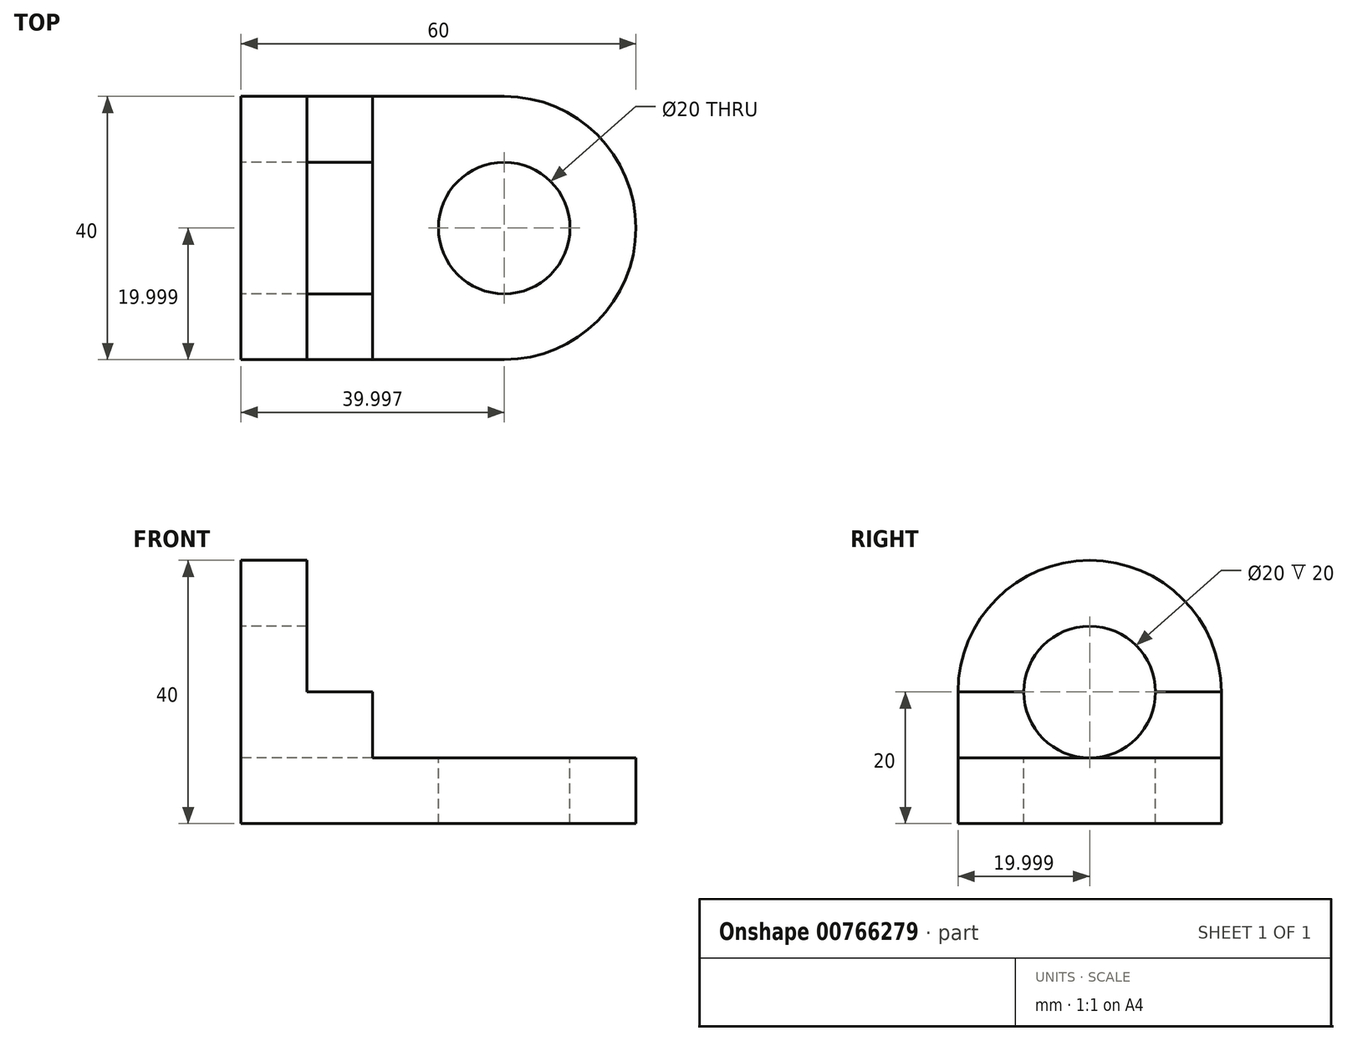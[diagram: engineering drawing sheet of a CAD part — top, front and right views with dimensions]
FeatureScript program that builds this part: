
annotation { "Feature Type Name" : "Feature", "Feature Type Description" : "" }
export const myFeature = defineFeature(function(context is Context, id is Id, definition is map)
    precondition{}
    {
        {
            var Q0;
            Q0=qCreatedBy(makeId("Top.planeOp"),FACE);
            var sketch = newSketch(context, id + "F0", { "sketchPlane" : qUnion([Q0])});
            skLineSegment(sketch, "E0.bottom", {"start": v(-26.43, 18.86) * mm, "end": v(33.57, 18.86) * mm});
            skLineSegment(sketch, "E0.top", {"start": v(-26.43, -21.14) * mm, "end": v(33.57, -21.14) * mm});
            skLineSegment(sketch, "E0.left", {"start": v(-26.43, 18.86) * mm, "end": v(-26.43, -21.14) * mm});
            skLineSegment(sketch, "E0.right", {"start": v(33.57, 18.86) * mm, "end": v(33.57, -21.14) * mm});
            skSolve(sketch);
        }
        {
            var Q0;
            Q0=makeQuery(id+"F0.imprint","IMPRINT",FACE,{"disambiguationData":[TD([[makeQuery(id+"F0.imprint","IMPRINT",EDGE,{"derivedFrom":sQuery(id+"F0.wireOp",EDGE,"E0.bottom")}),-1.0]])]});
            extrude(context, id + "F1", {"entities" : qUnion([Q0]), "depth" : 10 * mm, "offsetDistance" : 25.4 * mm});
        }
        {
            var Q0;
            Q0=makeQuery(id+"F1.opExtrude","CAP_FACE",FACE,{"disambiguationData":[OSD([sQuery(id+"F0.wireOp",EDGE,"E0.bottom"),sQuery(id+"F0.wireOp",EDGE,"E0.top"),sQuery(id+"F0.wireOp",EDGE,"E0.left"),sQuery(id+"F0.wireOp",EDGE,"E0.right")])],"isStart":false});
            var sketch = newSketch(context, id + "F2", { "sketchPlane" : qUnion([Q0])});
            skLineSegment(sketch, "E1", {"start": v(33.57, -1.14) * mm, "end": v(13.57, -1.14) * mm});
            skCircle(sketch, "E2", {"center": v(13.57, -1.14) * mm, "radius": 10 * mm});
            skSolve(sketch);
        }
        {
            var Q0;
            Q0=makeQuery(id+"F2.imprint","IMPRINT",FACE,{"disambiguationData":[TD([[makeQuery(id+"F2.imprint","IMPRINT",EDGE,{"derivedFrom":sQuery(id+"F2.wireOp",EDGE,"E2")}),1.0]])]});
            extrude(context, id + "F3", {"entities" : qUnion([Q0]), "operationType" : NewBodyOperationType.REMOVE, "oppositeDirection" : true, "depth" : 10 * mm, "offsetDistance" : 25.4 * mm});
        }
        {
            var Q0;
            Q0=makeQuery(id+"F1.opExtrude","SWEPT_EDGE",EDGE,{"disambiguationData":[OSD([sQuery(id+"F0.wireOp",EDGE,"E0.bottom"),sQuery(id+"F0.wireOp",EDGE,"E0.right")])]});
            var Q1;
            Q1=makeQuery(id+"F1.opExtrude","SWEPT_EDGE",EDGE,{"disambiguationData":[OSD([sQuery(id+"F0.wireOp",EDGE,"E0.top"),sQuery(id+"F0.wireOp",EDGE,"E0.right")])]});
            fillet(context, id + "F4", {"entities" : qUnion([Q0, Q1]), "radius" : 20 * mm, "tangentPropagation" : true, "allowEdgeOverflow" : false});
        }
        {
            var Q0;
            Q0=makeQuery(id+"F1.opExtrude","CAP_FACE",FACE,{"disambiguationData":[OSD([sQuery(id+"F0.wireOp",EDGE,"E0.bottom"),sQuery(id+"F0.wireOp",EDGE,"E0.top"),sQuery(id+"F0.wireOp",EDGE,"E0.left"),sQuery(id+"F0.wireOp",EDGE,"E0.right")])],"isStart":false});
            var sketch = newSketch(context, id + "F5", { "sketchPlane" : qUnion([Q0])});
            skLineSegment(sketch, "E3.bottom", {"start": v(-26.43, 18.86) * mm, "end": v(-6.43, 18.86) * mm});
            skLineSegment(sketch, "E3.top", {"start": v(-26.43, -21.14) * mm, "end": v(-6.43, -21.14) * mm});
            skLineSegment(sketch, "E3.left", {"start": v(-26.43, 18.86) * mm, "end": v(-26.43, -21.14) * mm});
            skLineSegment(sketch, "E3.right", {"start": v(-6.43, 18.86) * mm, "end": v(-6.43, -21.14) * mm});
            skSolve(sketch);
        }
        {
            var Q0;
            Q0=makeQuery(id+"F5.imprint","IMPRINT",FACE,{"disambiguationData":[TD([[makeQuery(id+"F5.imprint","IMPRINT",EDGE,{"derivedFrom":sQuery(id+"F5.wireOp",EDGE,"E3.bottom")}),-1.0]])]});
            extrude(context, id + "F6", {"entities" : qUnion([Q0]), "operationType" : NewBodyOperationType.ADD, "depth" : 10 * mm, "offsetDistance" : 25.4 * mm});
        }
        {
            var Q0;
            Q0=makeQuery(id+"F6.opExtrude","CAP_FACE",FACE,{"disambiguationData":[OSD([sQuery(id+"F5.wireOp",EDGE,"E3.bottom"),sQuery(id+"F5.wireOp",EDGE,"E3.top"),sQuery(id+"F5.wireOp",EDGE,"E3.left"),sQuery(id+"F5.wireOp",EDGE,"E3.right")])],"isStart":false});
            var sketch = newSketch(context, id + "F7", { "sketchPlane" : qUnion([Q0])});
            skLineSegment(sketch, "E4.bottom", {"start": v(-26.43, 18.86) * mm, "end": v(-16.43, 18.86) * mm});
            skLineSegment(sketch, "E4.top", {"start": v(-26.43, -21.14) * mm, "end": v(-16.43, -21.14) * mm});
            skLineSegment(sketch, "E4.left", {"start": v(-26.43, 18.86) * mm, "end": v(-26.43, -21.14) * mm});
            skLineSegment(sketch, "E4.right", {"start": v(-16.43, 18.86) * mm, "end": v(-16.43, -21.14) * mm});
            skSolve(sketch);
        }
        {
            var Q0;
            Q0=makeQuery(id+"F7.imprint","IMPRINT",FACE,{"disambiguationData":[TD([[makeQuery(id+"F7.imprint","IMPRINT",EDGE,{"derivedFrom":sQuery(id+"F7.wireOp",EDGE,"E4.bottom")}),-1.0]])]});
            extrude(context, id + "F8", {"entities" : qUnion([Q0]), "operationType" : NewBodyOperationType.ADD, "depth" : 20 * mm, "offsetDistance" : 25.4 * mm});
        }
        {
            var Q0;
            Q0=makeQuery(id+"F8.boolean.opBoolean","MERGE",FACE,{"derivedFrom":[makeQuery(id+"F6.boolean.opBoolean","MERGE",FACE,{"derivedFrom":[makeQuery(id+"F1.opExtrude","SWEPT_FACE",FACE,{"disambiguationData":[OSD([sQuery(id+"F0.wireOp",EDGE,"E0.left")])]}),makeQuery(id+"F6.opExtrude","SWEPT_FACE",FACE,{"disambiguationData":[OSD([sQuery(id+"F5.wireOp",EDGE,"E3.left")])]})]}),makeQuery(id+"F8.opExtrude","SWEPT_FACE",FACE,{"disambiguationData":[OSD([sQuery(id+"F7.wireOp",EDGE,"E4.left")])]})]});
            var sketch = newSketch(context, id + "F9", { "sketchPlane" : qUnion([Q0])});
            skCircle(sketch, "E5", {"center": v(1.14, 20) * mm, "radius": 10 * mm});
            skPoint(sketch, "E5.centerSnap0", {"position": v(21.14, 20) * mm});
            skPoint(sketch, "E5.centerSnap1", {"position": v(1.14, 40) * mm});
            skSolve(sketch);
        }
        {
            var Q0;
            Q0=makeQuery(id+"F9.imprint","IMPRINT",FACE,{"disambiguationData":[TD([[makeQuery(id+"F9.imprint","IMPRINT",EDGE,{"derivedFrom":sQuery(id+"F9.wireOp",EDGE,"E5")}),1.0]])]});
            extrude(context, id + "F10", {"entities" : qUnion([Q0]), "operationType" : NewBodyOperationType.REMOVE, "oppositeDirection" : true, "depth" : 20 * mm, "offsetDistance" : 25.4 * mm});
        }
        {
            var Q0;
            Q0=makeQuery(id+"F8.opExtrude","CAP_EDGE",EDGE,{"disambiguationData":[OSD([sQuery(id+"F7.wireOp",EDGE,"E4.top")])],"isStart":false});
            var Q1;
            Q1=makeQuery(id+"F8.opExtrude","CAP_EDGE",EDGE,{"disambiguationData":[OSD([sQuery(id+"F7.wireOp",EDGE,"E4.bottom")])],"isStart":false});
            fillet(context, id + "F11", {"entities" : qUnion([Q0, Q1]), "radius" : 20 * mm, "tangentPropagation" : true, "allowEdgeOverflow" : false});
        }
    });
